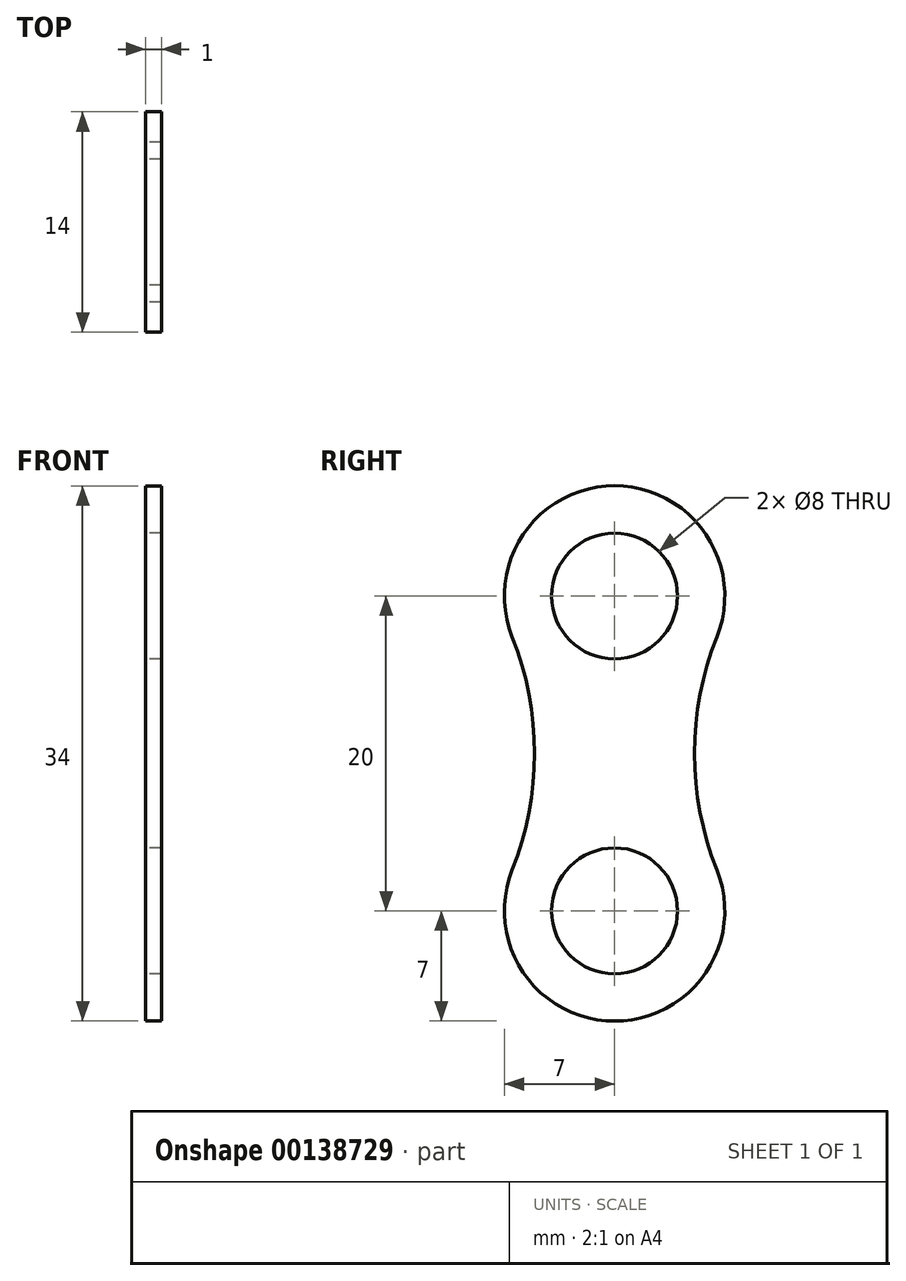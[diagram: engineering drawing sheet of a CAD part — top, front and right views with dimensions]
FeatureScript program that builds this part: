
annotation { "Feature Type Name" : "Feature", "Feature Type Description" : "" }
export const myFeature = defineFeature(function(context is Context, id is Id, definition is map)
    precondition{}
    {
        {
            var Q0;
            Q0=qCreatedBy(makeId("Right.planeOp"),FACE);
            var sketch = newSketch(context, id + "F0", { "sketchPlane" : qUnion([Q0])});
            skArc(sketch, "E0", {"start": v(6.5, 7.4) * mm, "mid": v(0, 17) * mm, "end": v(-6.5, 7.4) * mm});
            skArc(sketch, "E1", {"start": v(-6.5, -7.4) * mm, "mid": v(0, -17) * mm, "end": v(6.5, -7.4) * mm});
            skArc(sketch, "E2", {"start": v(-6.5, -7.4) * mm, "mid": v(-5.08, 0) * mm, "end": v(-6.5, 7.4) * mm});
            skArc(sketch, "E3", {"start": v(6.5, 7.4) * mm, "mid": v(5.08, 0) * mm, "end": v(6.5, -7.4) * mm});
            skCircle(sketch, "E4", {"center": v(0, 10) * mm, "radius": 4 * mm});
            skCircle(sketch, "E5", {"center": v(0, -10) * mm, "radius": 4 * mm});
            skSolve(sketch);
        }
        {
            var Q0;
            Q0=makeQuery(id+"F0.imprint","IMPRINT",FACE,{"disambiguationData":[TD([[makeQuery(id+"F0.imprint","IMPRINT",EDGE,{"derivedFrom":sQuery(id+"F0.wireOp",EDGE,"E0")}),1.0]])]});
            extrude(context, id + "F1", {"entities" : qUnion([Q0]), "depth" : 1 * mm});
        }
    });
